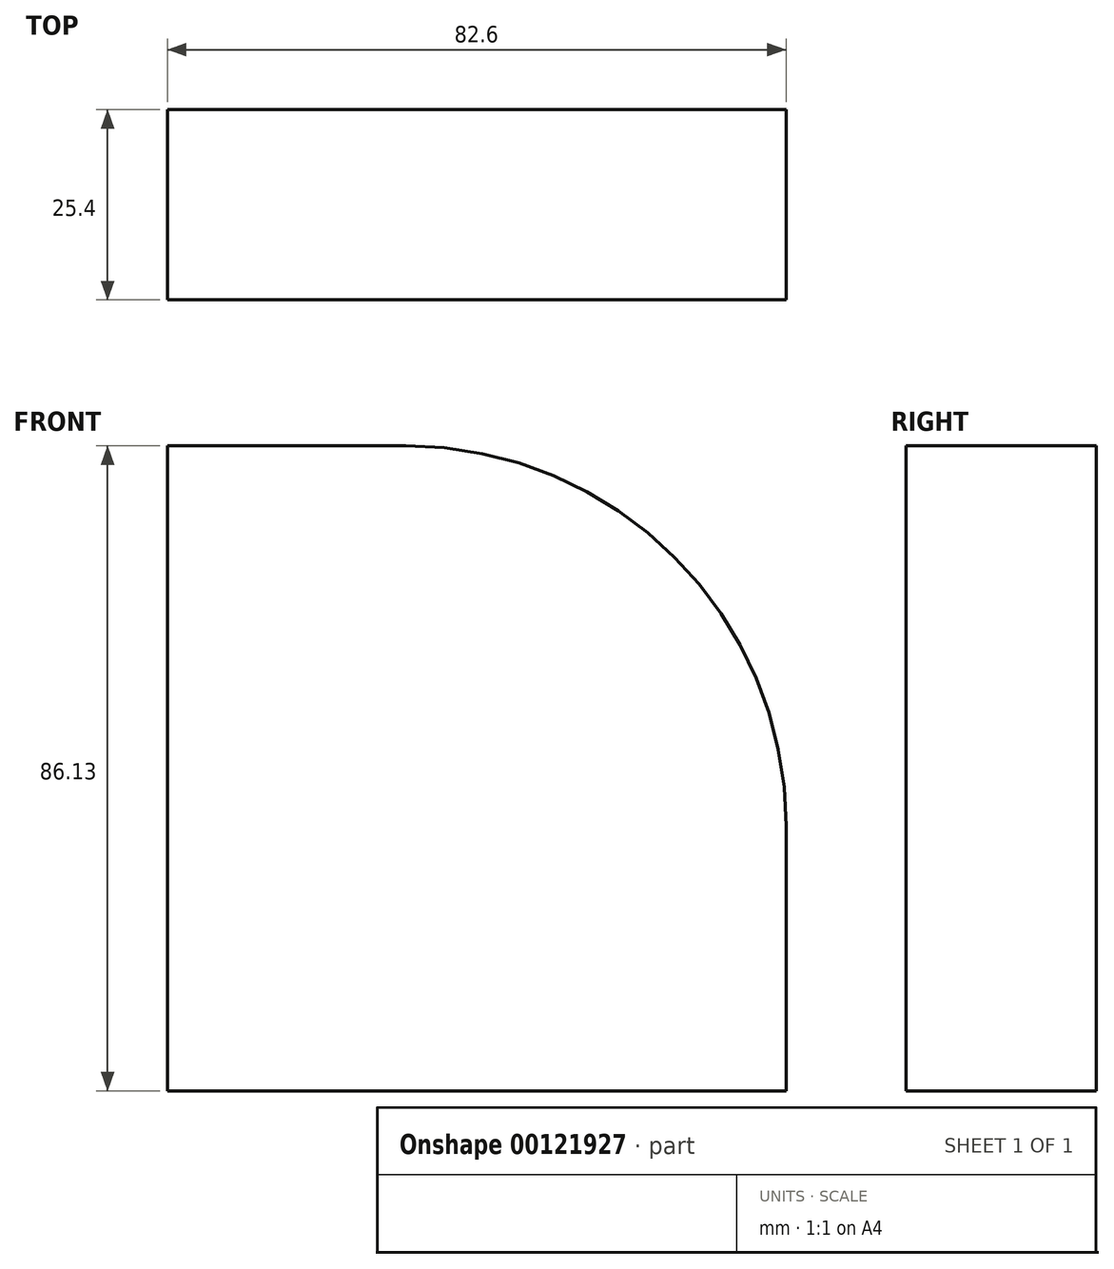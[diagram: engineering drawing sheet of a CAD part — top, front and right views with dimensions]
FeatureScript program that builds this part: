
annotation { "Feature Type Name" : "Feature", "Feature Type Description" : "" }
export const myFeature = defineFeature(function(context is Context, id is Id, definition is map)
    precondition{}
    {
        {
            var Q0;
            Q0=qCreatedBy(makeId("Front.planeOp"),FACE);
            var sketch = newSketch(context, id + "F0", { "sketchPlane" : qUnion([Q0])});
            skLineSegment(sketch, "E0.bottom", {"start": v(-64.05, -14.51) * mm, "end": v(-146.65, -14.51) * mm});
            skLineSegment(sketch, "E0.top", {"start": v(-64.05, -100.64) * mm, "end": v(-146.65, -100.64) * mm});
            skLineSegment(sketch, "E0.left", {"start": v(-64.05, -14.51) * mm, "end": v(-64.05, -100.64) * mm});
            skLineSegment(sketch, "E0.right", {"start": v(-146.65, -14.51) * mm, "end": v(-146.65, -100.64) * mm});
            skSolve(sketch);
        }
        {
            var Q0;
            Q0 = qSketchRegion(id + "F0", true);
            extrude(context, id + "F1", {"entities" : qUnion([Q0]), "depth" : 25.4 * mm});
        }
        {
            var Q0;
            Q0=makeQuery(id+"F1.opExtrude","SWEPT_EDGE",EDGE,{"disambiguationData":[OSD([sQuery(id+"F0.wireOp",EDGE,"E0.bottom"),sQuery(id+"F0.wireOp",EDGE,"E0.left")])]});
            fillet(context, id + "F2", {"entities" : qUnion([Q0]), "radius" : 50.8 * mm, "tangentPropagation" : true, "allowEdgeOverflow" : false});
        }
    });
